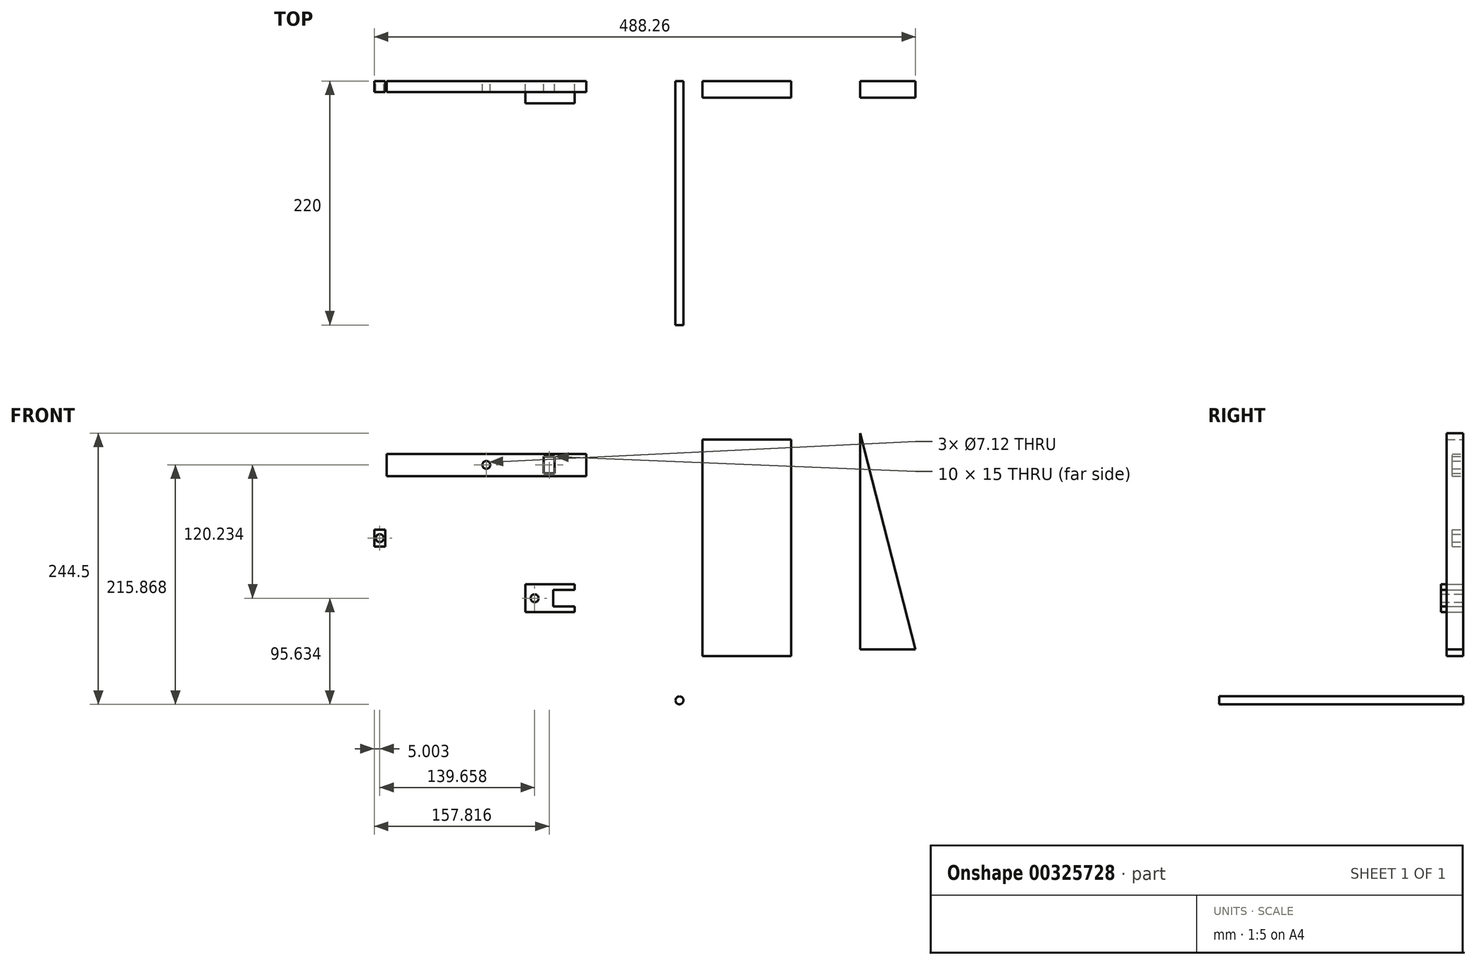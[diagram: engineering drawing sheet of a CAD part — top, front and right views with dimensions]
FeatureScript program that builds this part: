
annotation { "Feature Type Name" : "Feature", "Feature Type Description" : "" }
export const myFeature = defineFeature(function(context is Context, id is Id, definition is map)
    precondition{}
    {
        {
            var Q0;
            Q0=qCreatedBy(makeId("Front.planeOp"),FACE);
            var sketch = newSketch(context, id + "F0", { "sketchPlane" : qUnion([Q0])});
            skPoint(sketch, "E0", {"position": v(-253.7, 58.73) * mm});
            skPoint(sketch, "E1", {"position": v(-253.7, 33.54) * mm});
            skPoint(sketch, "E2", {"position": v(-217.64, 33.54) * mm});
            skPoint(sketch, "E3", {"position": v(-217.64, 58.73) * mm});
            skPoint(sketch, "E4", {"position": v(-217.64, 53.63) * mm});
            skPoint(sketch, "E5", {"position": v(-217.64, 38.63) * mm});
            skPoint(sketch, "E6", {"position": v(-236.98, 38.63) * mm});
            skPoint(sketch, "E7", {"position": v(-236.98, 53.63) * mm});
            skLineSegment(sketch, "E8", {"start": v(-217.64, 38.63) * mm, "end": v(-217.64, 33.54) * mm});
            skLineSegment(sketch, "E9", {"start": v(-217.64, 33.54) * mm, "end": v(-253.7, 33.54) * mm});
            skLineSegment(sketch, "E10", {"start": v(-236.98, 38.63) * mm, "end": v(-217.64, 38.63) * mm});
            skLineSegment(sketch, "E11", {"start": v(-236.98, 38.63) * mm, "end": v(-236.98, 53.63) * mm});
            skLineSegment(sketch, "E12", {"start": v(-236.98, 53.63) * mm, "end": v(-217.64, 53.63) * mm});
            skLineSegment(sketch, "E13", {"start": v(-217.64, 58.73) * mm, "end": v(-217.64, 53.63) * mm});
            skLineSegment(sketch, "E14", {"start": v(-217.64, 58.73) * mm, "end": v(-253.7, 58.73) * mm});
            skPoint(sketch, "E15", {"position": v(-253.7, 46.13) * mm});
            skLineSegment(sketch, "E16", {"start": v(-253.7, 58.73) * mm, "end": v(-253.7, 33.54) * mm});
            skLineSegment(sketch, "E17", {"start": v(-253.7, 46.13) * mm, "end": v(-253.7, 58.73) * mm});
            skLineSegment(sketch, "E18", {"start": v(-253.7, 46.13) * mm, "end": v(-253.7, 33.54) * mm});
            skCircle(sketch, "E19", {"center": v(-253.7, 46.13) * mm, "radius": 3.56 * mm});
            skPoint(sketch, "E20", {"position": v(-266.3, 46.13) * mm});
            skPoint(sketch, "E21", {"position": v(-261.99, 33.54) * mm});
            skPoint(sketch, "E22", {"position": v(-261.99, 58.73) * mm});
            skLineSegment(sketch, "E23", {"start": v(-261.99, 33.54) * mm, "end": v(-253.7, 33.54) * mm});
            skLineSegment(sketch, "E24", {"start": v(-261.99, 33.54) * mm, "end": v(-261.99, 58.73) * mm});
            skLineSegment(sketch, "E25", {"start": v(-253.7, 58.73) * mm, "end": v(-261.99, 58.73) * mm});
            skCircle(sketch, "E26", {"center": v(-123.08, -45.94) * mm, "radius": 3.56 * mm});
            skLineSegment(sketch, "E27.bottom", {"start": v(-207.25, 156.37) * mm, "end": v(-387.25, 156.37) * mm});
            skLineSegment(sketch, "E27.top", {"start": v(-207.25, 176.37) * mm, "end": v(-387.25, 176.37) * mm});
            skLineSegment(sketch, "E27.left", {"start": v(-207.25, 156.37) * mm, "end": v(-207.25, 176.37) * mm});
            skLineSegment(sketch, "E27.right", {"start": v(-387.25, 156.37) * mm, "end": v(-387.25, 176.37) * mm});
            skPoint(sketch, "E27.middle", {"position": v(-297.25, 166.37) * mm});
            skCircle(sketch, "E28", {"center": v(-297.25, 166.37) * mm, "radius": 3.56 * mm});
            skLineSegment(sketch, "E29.bottom", {"start": v(-388.36, 92.8) * mm, "end": v(-398.36, 92.8) * mm});
            skLineSegment(sketch, "E29.top", {"start": v(-388.36, 107.8) * mm, "end": v(-398.36, 107.8) * mm});
            skLineSegment(sketch, "E29.left", {"start": v(-388.36, 92.8) * mm, "end": v(-388.36, 107.8) * mm});
            skLineSegment(sketch, "E29.right", {"start": v(-398.36, 92.8) * mm, "end": v(-398.36, 107.8) * mm});
            skPoint(sketch, "E29.middle", {"position": v(-393.36, 100.3) * mm});
            skCircle(sketch, "E30", {"center": v(-393.36, 100.3) * mm, "radius": 3.56 * mm});
            skPoint(sketch, "E31", {"position": v(0, 0) * mm});
            skPoint(sketch, "E32", {"position": v(39.9, 0) * mm});
            skPoint(sketch, "E33", {"position": v(89.9, 0) * mm});
            skPoint(sketch, "E34", {"position": v(39.9, 195) * mm});
            skLineSegment(sketch, "E35", {"start": v(39.9, 195) * mm, "end": v(39.9, 0) * mm});
            skLineSegment(sketch, "E36", {"start": v(39.9, 195) * mm, "end": v(89.9, 0) * mm});
            skLineSegment(sketch, "E37", {"start": v(39.9, 0) * mm, "end": v(89.9, 0) * mm});
            skLineSegment(sketch, "E38.bottom", {"start": v(-22.33, -5.9) * mm, "end": v(-102.33, -5.9) * mm});
            skLineSegment(sketch, "E38.top", {"start": v(-22.33, 189.1) * mm, "end": v(-102.33, 189.1) * mm});
            skLineSegment(sketch, "E38.left", {"start": v(-22.33, -5.9) * mm, "end": v(-22.33, 189.1) * mm});
            skLineSegment(sketch, "E38.right", {"start": v(-102.33, -5.9) * mm, "end": v(-102.33, 189.1) * mm});
            skPoint(sketch, "E38.middle", {"position": v(-62.33, 91.6) * mm});
            skPoint(sketch, "E39", {"position": v(-62.33, 189.1) * mm});
            skPoint(sketch, "E40", {"position": v(-67.33, 189.1) * mm});
            skPoint(sketch, "E41", {"position": v(-57.33, 189.1) * mm});
            skLineSegment(sketch, "E42", {"start": v(-67.33, 189.1) * mm, "end": v(-62.33, 189.1) * mm});
            skLineSegment(sketch, "E43", {"start": v(-57.33, 189.1) * mm, "end": v(-62.33, 189.1) * mm});
            skLineSegment(sketch, "E44", {"start": v(-67.33, 189.1) * mm, "end": v(-67.33, 234.46) * mm});
            skLineSegment(sketch, "E45", {"start": v(-57.33, 189.1) * mm, "end": v(-57.33, 234.46) * mm});
            skLineSegment(sketch, "E46", {"start": v(-67.33, 234.46) * mm, "end": v(-57.33, 234.46) * mm});
            skPoint(sketch, "E47", {"position": v(-240.54, 166.37) * mm});
            skLineSegment(sketch, "E48.bottom", {"start": v(-245.54, 158.87) * mm, "end": v(-235.54, 158.87) * mm});
            skLineSegment(sketch, "E48.top", {"start": v(-245.54, 173.87) * mm, "end": v(-235.54, 173.87) * mm});
            skLineSegment(sketch, "E48.left", {"start": v(-245.54, 158.87) * mm, "end": v(-245.54, 173.87) * mm});
            skLineSegment(sketch, "E48.right", {"start": v(-235.54, 158.87) * mm, "end": v(-235.54, 173.87) * mm});
            skSolve(sketch);
        }
        {
            var Q0;
            {var subQ0=sQuery(id+"F0.wireOp",EDGE,"U1JqbFyr-VXk9-xrAh-nipi-QUNbOQzGi0AU");Q0=makeQuery(id+"F0.imprint","IMPRINT",FACE,{"disambiguationData":[TD([[makeQuery(id+"F0.imprint","IMPRINT",EDGE,{"derivedFrom":subQ0}),1.0]])]});}
            var Q1;
            Q1=makeQuery(id+"F0.imprint","IMPRINT",FACE,{"disambiguationData":[TD([[makeQuery(id+"F0.imprint","IMPRINT",EDGE,{"derivedFrom":sQuery(id+"F0.wireOp",EDGE,"E8")}),-1.0]])]});
            var Q2;
            {var subQ5=sQuery(id+"F0.wireOp",EDGE,"E23");Q2=makeQuery(id+"F0.imprint","IMPRINT",FACE,{"disambiguationData":[TD([[makeQuery(id+"F0.imprint","IMPRINT",EDGE,{"derivedFrom":subQ5}),1.0]])]});}
            extrude(context, id + "F1", {"entities" : qUnion([Q0, Q1, Q2]), "depth" : 20 * mm});
        }
        {
            var Q0;
            Q0=makeQuery(id+"F0.imprint","IMPRINT",FACE,{"disambiguationData":[TD([[makeQuery(id+"F0.imprint","IMPRINT",EDGE,{"derivedFrom":sQuery(id+"F0.wireOp",EDGE,"E26")}),1.0]])]});
            extrude(context, id + "F2", {"entities" : qUnion([Q0]), "depth" : 220 * mm});
        }
        {
            var Q0;
            Q0=makeQuery(id+"F0.imprint","IMPRINT",FACE,{"disambiguationData":[TD([[makeQuery(id+"F0.imprint","IMPRINT",EDGE,{"derivedFrom":sQuery(id+"F0.wireOp",EDGE,"E27.bottom")}),-1.0]])]});
            extrude(context, id + "F3", {"entities" : qUnion([Q0]), "depth" : 10 * mm});
        }
        {
            var Q0;
            Q0=makeQuery(id+"F0.imprint","IMPRINT",FACE,{"disambiguationData":[TD([[makeQuery(id+"F0.imprint","IMPRINT",EDGE,{"derivedFrom":sQuery(id+"F0.wireOp",EDGE,"E29.bottom")}),-1.0]])]});
            extrude(context, id + "F4", {"entities" : qUnion([Q0]), "depth" : 10 * mm});
        }
        {
            var Q0;
            Q0=makeQuery(id+"F0.imprint","IMPRINT",FACE,{"disambiguationData":[TD([[makeQuery(id+"F0.imprint","IMPRINT",EDGE,{"derivedFrom":sQuery(id+"F0.wireOp",EDGE,"E38.bottom")}),-1.0]])]});
            var Q1;
            Q1=makeQuery(id+"F0.imprint","IMPRINT",FACE,{"disambiguationData":[TD([[makeQuery(id+"F0.imprint","IMPRINT",EDGE,{"derivedFrom":sQuery(id+"F0.wireOp",EDGE,"E42")}),1.0]])]});
            var Q2;
            Q2=makeQuery(id+"F0.imprint","IMPRINT",FACE,{"disambiguationData":[TD([[makeQuery(id+"F0.imprint","IMPRINT",EDGE,{"derivedFrom":sQuery(id+"F0.wireOp",EDGE,"E35")}),1.0]])]});
            extrude(context, id + "F5", {"entities" : qUnion([Q0, Q1, Q2]), "depth" : 15 * mm});
        }
        {
            var Q0;
            Q0=makeQuery(id+"F0.imprint","IMPRINT",FACE,{"disambiguationData":[TD([[makeQuery(id+"F0.imprint","IMPRINT",EDGE,{"derivedFrom":sQuery(id+"F0.wireOp",EDGE,"E35")}),1.0]])]});
            extrude(context, id + "F6", {"entities" : qUnion([Q0]), "depth" : 15 * mm});
        }
    });
